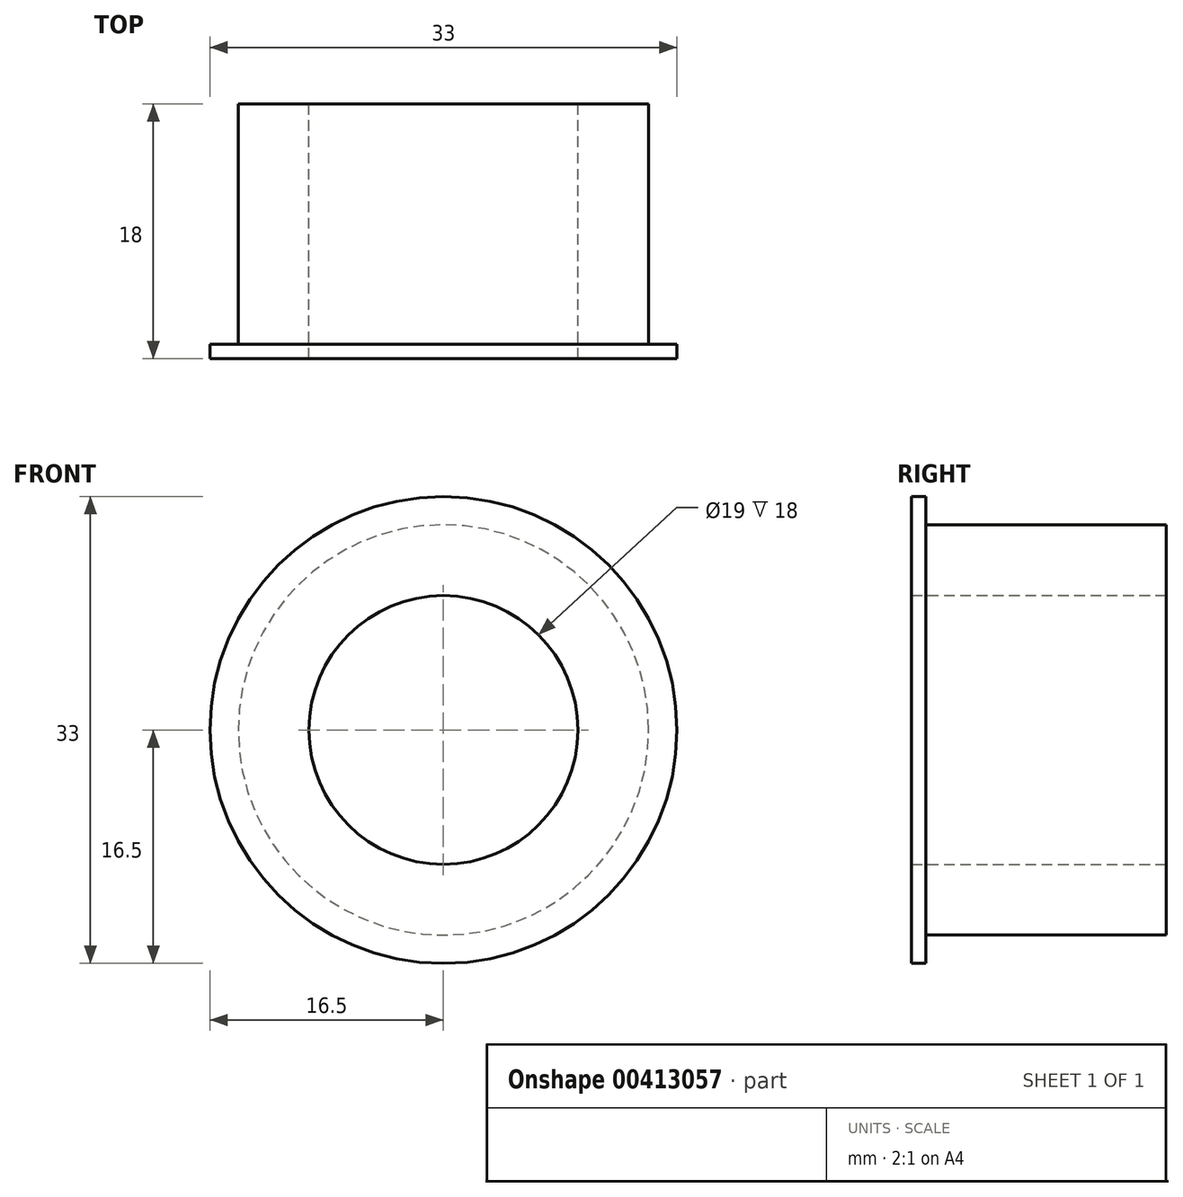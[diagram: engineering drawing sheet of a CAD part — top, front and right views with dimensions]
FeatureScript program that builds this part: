
annotation { "Feature Type Name" : "Feature", "Feature Type Description" : "" }
export const myFeature = defineFeature(function(context is Context, id is Id, definition is map)
    precondition{}
    {
        {
            var Q0;
            Q0=qCreatedBy(makeId("Front.planeOp"),FACE);
            var sketch = newSketch(context, id + "F0", { "sketchPlane" : qUnion([Q0])});
            skCircle(sketch, "E0", {"center": v(0, 0) * mm, "radius": 14.5 * mm});
            skCircle(sketch, "E1", {"center": v(0, 0) * mm, "radius": 9.5 * mm});
            skCircle(sketch, "E2", {"center": v(0, 0) * mm, "radius": 16.5 * mm});
            skSolve(sketch);
        }
        {
            var Q0;
            Q0=makeQuery(id+"F0.imprint","IMPRINT",FACE,{"disambiguationData":[TD([[makeQuery(id+"F0.imprint","IMPRINT",EDGE,{"derivedFrom":sQuery(id+"F0.wireOp",EDGE,"E0")}),-1.0]])]});
            var Q1;
            Q1=makeQuery(id+"F0.imprint","IMPRINT",FACE,{"disambiguationData":[TD([[makeQuery(id+"F0.imprint","IMPRINT",EDGE,{"derivedFrom":sQuery(id+"F0.wireOp",EDGE,"E0")}),1.0]])]});
            extrude(context, id + "F1", {"entities" : qUnion([Q0, Q1]), "depth" : 1 * mm});
        }
        {
            var Q0;
            Q0=makeQuery(id+"F0.imprint","IMPRINT",FACE,{"disambiguationData":[TD([[makeQuery(id+"F0.imprint","IMPRINT",EDGE,{"derivedFrom":sQuery(id+"F0.wireOp",EDGE,"E0")}),1.0]])]});
            extrude(context, id + "F2", {"entities" : qUnion([Q0]), "operationType" : NewBodyOperationType.ADD, "oppositeDirection" : true, "depth" : 17 * mm});
        }
    });
